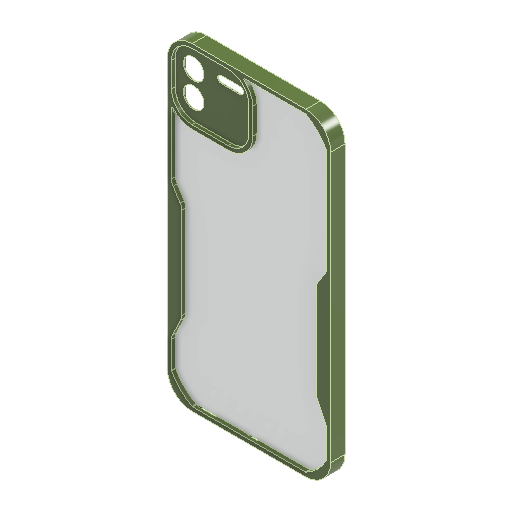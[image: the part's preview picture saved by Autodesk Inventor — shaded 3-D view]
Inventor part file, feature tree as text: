
AUTODESK INVENTOR PART (.ipt)
format: ipt  version: 2025.2 (Build 292293000, 293)  size: 374,272 bytes
history: native  units: mm
features: extrude x13, sketch x6, plane x2, projected_geometry x2
ambient origin geometry x8: Origin, YZ Plane, XZ Plane, XY Plane, X Axis, Y Axis, Z Axis, Center Point
bodies: Solid1 (feature_tree)
feature tree (23):
  sketch  "Sketch1"  dims[d3=10.0mm d4=10.0mm]
  extrude  "Extrusion1"  Depth=10.0mm
  extrude  "Extrusion2"  Depth=10.0mm
  extrude  "Extrusion3"  Depth=5.0mm
  extrude  "Extrusion4"  Depth=5.0mm
  extrude  "Extrusion5"  Depth=0.5mm
  extrude  "Extrusion6"  Depth=0.5mm
  sketch  "Sketch3"  dims[d10=10.0mm d12=5.0mm]
  extrude  "Extrusion7"  Depth=0.5mm
  extrude  "Extrusion8"  Depth=2.0mm TaperAngle=0.0deg
  extrude  "Extrusion9"  Depth=2.0mm TaperAngle=0.0deg
  extrude  "Extrusion10"  Depth=2.0mm TaperAngle=0.0deg
  extrude  "Extrusion11"  Depth=0.5mm TaperAngle=0.0deg
  extrude  "Extrusion12"  Depth=1.0mm TaperAngle=0.0deg
  sketch  "Sketch4"  dims[d13=5.0mm d14=5.0mm]
  sketch  "Sketch5"  dims[d15=2.0mm d16=0.5mm]
  plane  "Work Plane2"
  extrude  "Extrusion13"  Depth=2.0mm TaperAngle=0.0deg
  sketch  "Sketch2"  dims[d5=10.0mm d6=10.0mm d9=10.0mm]
  projected_geometry  "Projected Loop1"
  projected_geometry  "Projected Loop2"
  plane  "Work Plane1"
  sketch  "Sketch7"  dims[d17=0.5mm d18=0.5mm d19=0.5mm d20=2.0mm d21=5.0mm d22=0.0mm d23=0.0mm d24=2.0mm d25=0.0mm d26=2.0mm d27=0.0mm d28=0.5mm d29=0.0mm d30=1.0mm d31=0.0mm d32=2.0mm d33=0.0mm d34=2.0mm d35=0.0mm d36=0.2mm d37=0.0mm d38=0.2mm d39=0.0mm d40=0.2mm d41=0.0mm d42=0.2mm d43=0.0mm d44=0.2mm d45=0.0mm d46=1.0mm d47=55.0mm d48=27.5mm d49=27.5mm d50=2.516538mm d51=2.0mm d52=0.0mm]
